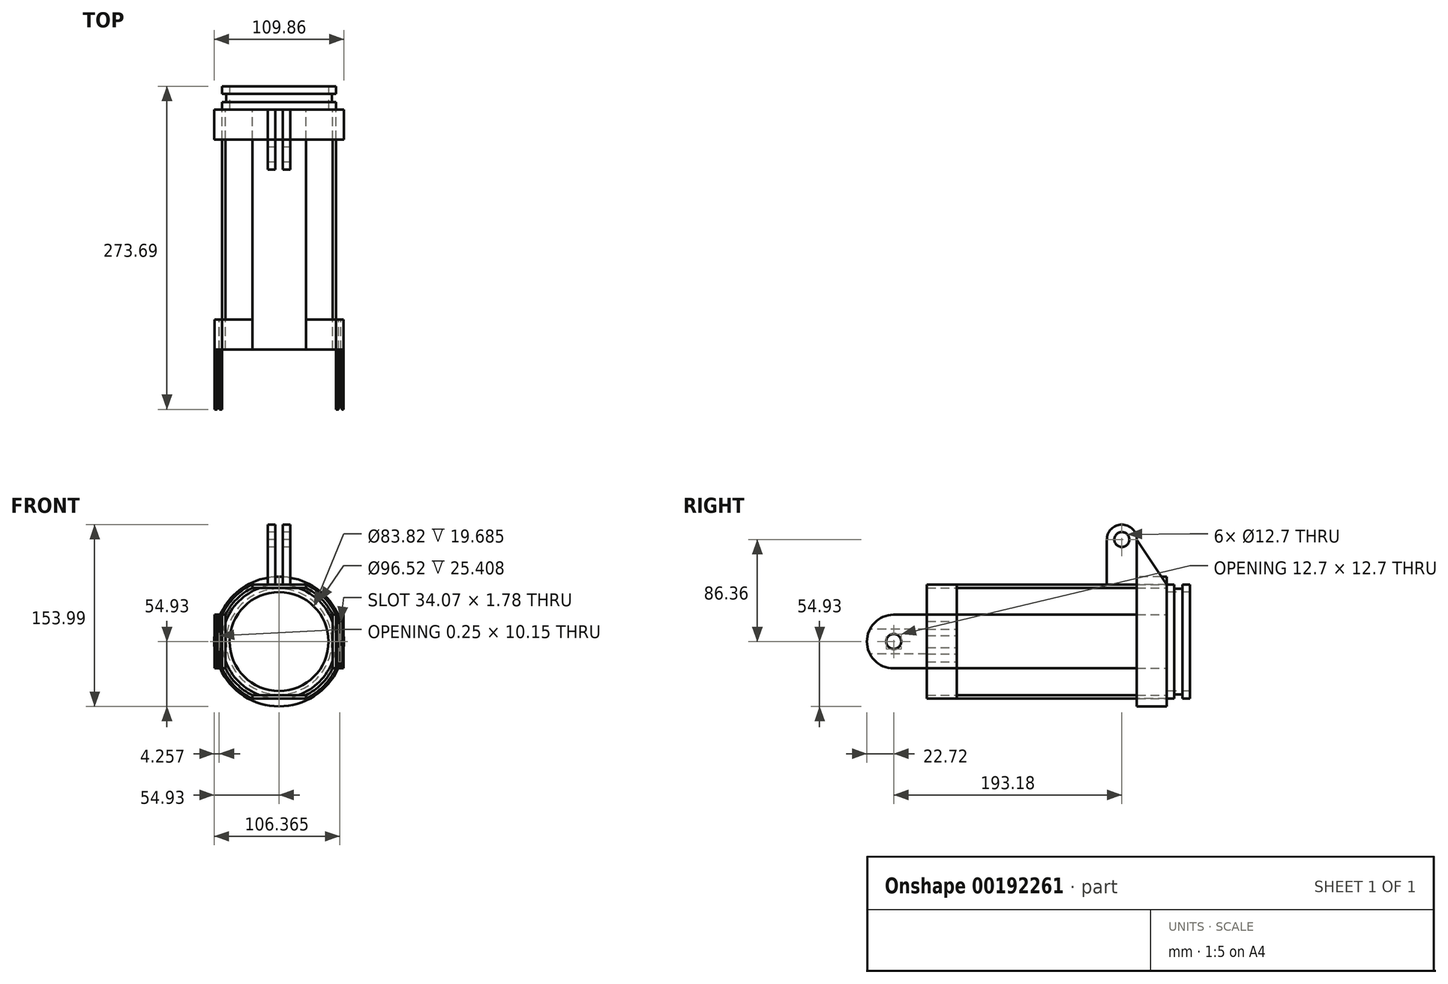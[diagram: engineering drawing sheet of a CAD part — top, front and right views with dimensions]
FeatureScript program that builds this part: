
annotation { "Feature Type Name" : "Feature", "Feature Type Description" : "" }
export const myFeature = defineFeature(function(context is Context, id is Id, definition is map)
    precondition{}
    {
        {
            var Q0;
            Q0=qCreatedBy(makeId("Front.planeOp"),FACE);
            var sketch = newSketch(context, id + "F0", { "sketchPlane" : qUnion([Q0])});
            skCircle(sketch, "E0", {"center": v(0, 0) * mm, "radius": 50.8 * mm});
            skCircle(sketch, "E1", {"center": v(0, 0) * mm, "radius": 53.34 * mm});
            skLineSegment(sketch, "E2", {"start": v(0, -48.26) * mm, "end": v(22.72, -48.26) * mm});
            skLineSegment(sketch, "E3", {"start": v(22.72, -48.26) * mm, "end": v(22.72, -45.44) * mm});
            skLineSegment(sketch, "E4", {"start": v(22.72, -45.44) * mm, "end": v(-22.72, -45.44) * mm});
            skLineSegment(sketch, "E5", {"start": v(-22.72, -45.44) * mm, "end": v(-22.72, -48.26) * mm});
            skLineSegment(sketch, "E6", {"start": v(-22.72, -48.26) * mm, "end": v(0, -48.26) * mm});
            skLineSegment(sketch, "E7", {"start": v(-48.26, 0) * mm, "end": v(-48.26, -22.72) * mm});
            skLineSegment(sketch, "E8", {"start": v(-48.26, -22.72) * mm, "end": v(-45.44, -22.72) * mm});
            skLineSegment(sketch, "E9", {"start": v(-45.44, -22.72) * mm, "end": v(-45.44, 22.72) * mm});
            skLineSegment(sketch, "E10", {"start": v(-45.44, 22.72) * mm, "end": v(-48.26, 22.72) * mm});
            skLineSegment(sketch, "E11", {"start": v(-48.26, 22.72) * mm, "end": v(-48.26, 0) * mm});
            skLineSegment(sketch, "E12", {"start": v(48.26, 0) * mm, "end": v(48.26, -22.72) * mm});
            skLineSegment(sketch, "E13", {"start": v(48.26, -22.72) * mm, "end": v(45.44, -22.72) * mm});
            skLineSegment(sketch, "E14", {"start": v(45.44, -22.72) * mm, "end": v(45.44, 22.72) * mm});
            skLineSegment(sketch, "E15", {"start": v(45.44, 22.72) * mm, "end": v(48.26, 22.72) * mm});
            skLineSegment(sketch, "E16", {"start": v(48.26, 22.72) * mm, "end": v(48.26, 0) * mm});
            skLineSegment(sketch, "E17", {"start": v(0, 50.8) * mm, "end": v(0, 48.26) * mm});
            skLineSegment(sketch, "E18", {"start": v(0, 48.26) * mm, "end": v(22.72, 48.26) * mm});
            skLineSegment(sketch, "E19", {"start": v(22.72, 48.26) * mm, "end": v(22.72, 45.44) * mm});
            skLineSegment(sketch, "E20", {"start": v(22.72, 45.44) * mm, "end": v(-22.72, 45.44) * mm});
            skLineSegment(sketch, "E21", {"start": v(-22.72, 45.44) * mm, "end": v(-22.72, 48.26) * mm});
            skLineSegment(sketch, "E22", {"start": v(-22.72, 48.26) * mm, "end": v(0, 48.26) * mm});
            skLineSegment(sketch, "E23", {"start": v(-48.26, -22.72) * mm, "end": v(-50.55, -22.72) * mm});
            skLineSegment(sketch, "E24", {"start": v(-50.55, -22.72) * mm, "end": v(-50.55, 22.72) * mm});
            skLineSegment(sketch, "E25", {"start": v(-50.55, 22.72) * mm, "end": v(-48.26, 22.72) * mm});
            skLineSegment(sketch, "E26", {"start": v(-50.55, 22.72) * mm, "end": v(-52.32, 22.72) * mm});
            skLineSegment(sketch, "E27", {"start": v(-52.32, 22.72) * mm, "end": v(-52.32, -22.72) * mm});
            skLineSegment(sketch, "E28", {"start": v(-52.32, -22.72) * mm, "end": v(-50.55, -22.72) * mm});
            skLineSegment(sketch, "E29", {"start": v(48.26, -22.72) * mm, "end": v(50.55, -22.72) * mm});
            skLineSegment(sketch, "E30", {"start": v(50.55, -22.72) * mm, "end": v(50.55, 22.72) * mm});
            skLineSegment(sketch, "E31", {"start": v(50.55, 22.72) * mm, "end": v(48.26, 22.72) * mm});
            skLineSegment(sketch, "E32", {"start": v(50.55, 22.72) * mm, "end": v(52.32, 22.72) * mm});
            skLineSegment(sketch, "E33", {"start": v(52.32, 22.72) * mm, "end": v(52.32, -22.72) * mm});
            skLineSegment(sketch, "E34", {"start": v(52.32, -22.72) * mm, "end": v(50.55, -22.72) * mm});
            skLineSegment(sketch, "E35", {"start": v(48.26, 0) * mm, "end": v(0, 0) * mm});
            skLineSegment(sketch, "E36.bottom", {"start": v(52.32, -22.72) * mm, "end": v(54.61, -22.72) * mm});
            skLineSegment(sketch, "E36.top", {"start": v(52.32, 22.72) * mm, "end": v(54.61, 22.72) * mm});
            skLineSegment(sketch, "E36.left", {"start": v(52.32, -22.72) * mm, "end": v(52.32, 22.72) * mm});
            skLineSegment(sketch, "E36.right", {"start": v(54.61, -22.72) * mm, "end": v(54.6, 22.72) * mm});
            skLineSegment(sketch, "E37.bottom", {"start": v(54.61, -22.72) * mm, "end": v(56.13, -22.72) * mm});
            skLineSegment(sketch, "E37.top", {"start": v(54.61, 22.72) * mm, "end": v(56.13, 22.72) * mm});
            skLineSegment(sketch, "E37.right", {"start": v(56.13, -22.72) * mm, "end": v(56.13, 22.72) * mm});
            skLineSegment(sketch, "E38.bottom", {"start": v(-52.32, 22.72) * mm, "end": v(-54.61, 22.72) * mm});
            skLineSegment(sketch, "E38.top", {"start": v(-52.32, -22.72) * mm, "end": v(-54.61, -22.72) * mm});
            skLineSegment(sketch, "E38.right", {"start": v(-54.61, 22.72) * mm, "end": v(-54.6, -22.72) * mm});
            skLineSegment(sketch, "E39.bottom", {"start": v(-54.61, 22.72) * mm, "end": v(-56.13, 22.72) * mm});
            skLineSegment(sketch, "E39.top", {"start": v(-54.61, -22.72) * mm, "end": v(-56.13, -22.72) * mm});
            skLineSegment(sketch, "E39.right", {"start": v(-56.13, 22.72) * mm, "end": v(-56.13, -22.72) * mm});
            skSolve(sketch);
        }
        {
            var Q0;
            {var subQ0=sQuery(id+"F0.wireOp",EDGE,"E5");Q0=makeQuery(id+"F0.imprint","IMPRINT",FACE,{"disambiguationData":[TD([[makeQuery(id+"F0.imprint","IMPRINT",EDGE,{"derivedFrom":subQ0}),-1.0]])]});}
            var Q1;
            {var subQ0=sQuery(id+"F0.wireOp",EDGE,"E3");Q1=makeQuery(id+"F0.imprint","IMPRINT",FACE,{"disambiguationData":[TD([[makeQuery(id+"F0.imprint","IMPRINT",EDGE,{"derivedFrom":subQ0}),-1.0]])]});}
            var Q2;
            {var subQ0=sQuery(id+"F0.wireOp",EDGE,"E10");Q2=makeQuery(id+"F0.imprint","IMPRINT",FACE,{"disambiguationData":[TD([[makeQuery(id+"F0.imprint","IMPRINT",EDGE,{"derivedFrom":subQ0}),-1.0]])]});}
            var Q3;
            {var subQ0=sQuery(id+"F0.wireOp",EDGE,"E15");Q3=makeQuery(id+"F0.imprint","IMPRINT",FACE,{"disambiguationData":[TD([[makeQuery(id+"F0.imprint","IMPRINT",EDGE,{"derivedFrom":subQ0}),1.0]])]});}
            extrude(context, id + "F1", {"entities" : qUnion([Q0, Q1, Q2, Q3]), "depth" : 25.4 * mm});
        }
        {
            var Q0;
            {var subQ0=sQuery(id+"F0.wireOp",EDGE,"E20");Q0=makeQuery(id+"F0.imprint","IMPRINT",FACE,{"disambiguationData":[TD([[makeQuery(id+"F0.imprint","IMPRINT",EDGE,{"derivedFrom":subQ0}),-1.0]])]});}
            var Q1;
            {var subQ0=sQuery(id+"F0.wireOp",EDGE,"E21");Q1=makeQuery(id+"F0.imprint","IMPRINT",FACE,{"disambiguationData":[TD([[makeQuery(id+"F0.imprint","IMPRINT",EDGE,{"derivedFrom":subQ0}),-1.0]])]});}
            var Q2;
            {var subQ0=sQuery(id+"F0.wireOp",EDGE,"E19");Q2=makeQuery(id+"F0.imprint","IMPRINT",FACE,{"disambiguationData":[TD([[makeQuery(id+"F0.imprint","IMPRINT",EDGE,{"derivedFrom":subQ0}),-1.0]])]});}
            var Q3;
            {var subQ0=sQuery(id+"F0.wireOp",EDGE,"E15");Q3=makeQuery(id+"F0.imprint","IMPRINT",FACE,{"disambiguationData":[TD([[makeQuery(id+"F0.imprint","IMPRINT",EDGE,{"derivedFrom":subQ0}),-1.0]])]});}
            var Q4;
            {var subQ5=sQuery(id+"F0.wireOp",EDGE,"E14");Q4=makeQuery(id+"F0.imprint","IMPRINT",FACE,{"disambiguationData":[TD([[makeQuery(id+"F0.imprint","IMPRINT",EDGE,{"derivedFrom":subQ5}),-1.0]])]});}
            var Q5;
            {var subQ0=sQuery(id+"F0.wireOp",EDGE,"E13");Q5=makeQuery(id+"F0.imprint","IMPRINT",FACE,{"disambiguationData":[TD([[makeQuery(id+"F0.imprint","IMPRINT",EDGE,{"derivedFrom":subQ0}),-1.0]])]});}
            var Q6;
            {var subQ0=sQuery(id+"F0.wireOp",EDGE,"E3");Q6=makeQuery(id+"F0.imprint","IMPRINT",FACE,{"disambiguationData":[TD([[makeQuery(id+"F0.imprint","IMPRINT",EDGE,{"derivedFrom":subQ0}),1.0]])]});}
            var Q7;
            {var subQ0=sQuery(id+"F0.wireOp",EDGE,"E4");Q7=makeQuery(id+"F0.imprint","IMPRINT",FACE,{"disambiguationData":[TD([[makeQuery(id+"F0.imprint","IMPRINT",EDGE,{"derivedFrom":subQ0}),1.0]])]});}
            var Q8;
            {var subQ0=sQuery(id+"F0.wireOp",EDGE,"E5");Q8=makeQuery(id+"F0.imprint","IMPRINT",FACE,{"disambiguationData":[TD([[makeQuery(id+"F0.imprint","IMPRINT",EDGE,{"derivedFrom":subQ0}),1.0]])]});}
            var Q9;
            {var subQ0=sQuery(id+"F0.wireOp",EDGE,"E8");Q9=makeQuery(id+"F0.imprint","IMPRINT",FACE,{"disambiguationData":[TD([[makeQuery(id+"F0.imprint","IMPRINT",EDGE,{"derivedFrom":subQ0}),1.0]])]});}
            var Q10;
            {var subQ0=sQuery(id+"F0.wireOp",EDGE,"E9");Q10=makeQuery(id+"F0.imprint","IMPRINT",FACE,{"disambiguationData":[TD([[makeQuery(id+"F0.imprint","IMPRINT",EDGE,{"derivedFrom":subQ0}),1.0]])]});}
            var Q11;
            {var subQ0=sQuery(id+"F0.wireOp",EDGE,"E10");Q11=makeQuery(id+"F0.imprint","IMPRINT",FACE,{"disambiguationData":[TD([[makeQuery(id+"F0.imprint","IMPRINT",EDGE,{"derivedFrom":subQ0}),1.0]])]});}
            extrude(context, id + "F2", {"entities" : qUnion([Q0, Q1, Q2, Q3, Q4, Q5, Q6, Q7, Q8, Q9, Q10, Q11]), "depth" : 203.2 * mm});
        }
        {
            var Q0;
            {var subQ0=sQuery(id+"F0.wireOp",EDGE,"E11");var subQ1=sQuery(id+"F0.wireOp",EDGE,"E0");var subQ2=makeQuery(id+"F0.imprint","INTERSECT",VERTEX,{"derivedFrom":[subQ1,subQ0]});Q0=makeQuery(id+"F0.imprint","IMPRINT",FACE,{"disambiguationData":[TD([[makeQuery(id+"F0.imprint","IMPRINT",EDGE,{"disambiguationData":[TD([[subQ2,-1.0]])],"derivedFrom":subQ1}),1.0]])]});}
            var Q1;
            {var subQ3=sQuery(id+"F0.wireOp",EDGE,"E0");var subQ6=sQuery(id+"F0.wireOp",EDGE,"E11");var subQ8=makeQuery(id+"F0.imprint","INTERSECT",VERTEX,{"derivedFrom":[subQ3,subQ6]});Q1=makeQuery(id+"F0.imprint","IMPRINT",FACE,{"disambiguationData":[TD([[makeQuery(id+"F0.imprint","IMPRINT",EDGE,{"disambiguationData":[TD([[subQ8,-1.0]])],"derivedFrom":subQ3}),-1.0]])]});}
            var Q2;
            {var subQ0=sQuery(id+"F0.wireOp",EDGE,"E26");Q2=makeQuery(id+"F0.imprint","IMPRINT",FACE,{"disambiguationData":[TD([[makeQuery(id+"F0.imprint","IMPRINT",EDGE,{"derivedFrom":subQ0}),1.0]])]});}
            var Q3;
            {var subQ0=sQuery(id+"F0.wireOp",EDGE,"E23");Q3=makeQuery(id+"F0.imprint","IMPRINT",FACE,{"disambiguationData":[TD([[makeQuery(id+"F0.imprint","IMPRINT",EDGE,{"derivedFrom":subQ0}),-1.0]])]});}
            var Q4;
            {var subQ0=sQuery(id+"F0.wireOp",EDGE,"E25");Q4=makeQuery(id+"F0.imprint","IMPRINT",FACE,{"disambiguationData":[TD([[makeQuery(id+"F0.imprint","IMPRINT",EDGE,{"derivedFrom":subQ0}),-1.0]])]});}
            var Q5;
            {var subQ0=sQuery(id+"F0.wireOp",EDGE,"E29");Q5=makeQuery(id+"F0.imprint","IMPRINT",FACE,{"disambiguationData":[TD([[makeQuery(id+"F0.imprint","IMPRINT",EDGE,{"derivedFrom":subQ0}),1.0]])]});}
            var Q6;
            {var subQ0=sQuery(id+"F0.wireOp",EDGE,"E32");Q6=makeQuery(id+"F0.imprint","IMPRINT",FACE,{"disambiguationData":[TD([[makeQuery(id+"F0.imprint","IMPRINT",EDGE,{"derivedFrom":subQ0}),-1.0]])]});}
            var Q7;
            {var subQ3=sQuery(id+"F0.wireOp",EDGE,"E0");var subQ6=sQuery(id+"F0.wireOp",EDGE,"E16");var subQ8=makeQuery(id+"F0.imprint","INTERSECT",VERTEX,{"derivedFrom":[subQ3,subQ6]});Q7=makeQuery(id+"F0.imprint","IMPRINT",FACE,{"disambiguationData":[TD([[makeQuery(id+"F0.imprint","IMPRINT",EDGE,{"disambiguationData":[TD([[subQ8,1.0]])],"derivedFrom":subQ3}),-1.0]])]});}
            var Q8;
            {var subQ0=sQuery(id+"F0.wireOp",EDGE,"E16");var subQ1=sQuery(id+"F0.wireOp",EDGE,"E0");var subQ2=makeQuery(id+"F0.imprint","INTERSECT",VERTEX,{"derivedFrom":[subQ1,subQ0]});Q8=makeQuery(id+"F0.imprint","IMPRINT",FACE,{"disambiguationData":[TD([[makeQuery(id+"F0.imprint","IMPRINT",EDGE,{"disambiguationData":[TD([[subQ2,1.0]])],"derivedFrom":subQ1}),1.0]])]});}
            var Q9;
            {var subQ0=sQuery(id+"F0.wireOp",EDGE,"E31");Q9=makeQuery(id+"F0.imprint","IMPRINT",FACE,{"disambiguationData":[TD([[makeQuery(id+"F0.imprint","IMPRINT",EDGE,{"derivedFrom":subQ0}),1.0]])]});}
            var Q10;
            {var subQ0=sQuery(id+"F0.wireOp",EDGE,"E1");var subQ1=makeQuery(id+"F0.imprint","INTERSECT",VERTEX,{"derivedFrom":[subQ0,sQuery(id+"F0.wireOp",EDGE,"E33")]});Q10=makeQuery(id+"F0.imprint","IMPRINT",FACE,{"disambiguationData":[TD([[makeQuery(id+"F0.imprint","IMPRINT",EDGE,{"disambiguationData":[TD([[subQ1,-1.0]])],"derivedFrom":subQ0}),1.0]])]});}
            var Q11;
            {var subQ0=sQuery(id+"F0.wireOp",EDGE,"E30");var subQ1=sQuery(id+"F0.wireOp",EDGE,"E0");var subQ2=makeQuery(id+"F0.imprint","INTERSECT",VERTEX,{"derivedFrom":[subQ1,subQ0]});Q11=makeQuery(id+"F0.imprint","IMPRINT",FACE,{"disambiguationData":[TD([[makeQuery(id+"F0.imprint","IMPRINT",EDGE,{"disambiguationData":[TD([[subQ2,1.0]])],"derivedFrom":subQ1}),-1.0]])]});}
            var Q12;
            {var subQ5=sQuery(id+"F0.wireOp",EDGE,"E34");Q12=makeQuery(id+"F0.imprint","IMPRINT",FACE,{"disambiguationData":[TD([[makeQuery(id+"F0.imprint","IMPRINT",EDGE,{"derivedFrom":subQ5}),-1.0]])]});}
            var Q13;
            {var subQ0=sQuery(id+"F0.wireOp",EDGE,"E24");var subQ1=sQuery(id+"F0.wireOp",EDGE,"E0");var subQ2=makeQuery(id+"F0.imprint","INTERSECT",VERTEX,{"derivedFrom":[subQ1,subQ0]});Q13=makeQuery(id+"F0.imprint","IMPRINT",FACE,{"disambiguationData":[TD([[makeQuery(id+"F0.imprint","IMPRINT",EDGE,{"disambiguationData":[TD([[subQ2,-1.0]])],"derivedFrom":subQ1}),-1.0]])]});}
            var Q14;
            {var subQ0=sQuery(id+"F0.wireOp",EDGE,"E1");var subQ1=makeQuery(id+"F0.imprint","INTERSECT",VERTEX,{"derivedFrom":[subQ0,sQuery(id+"F0.wireOp",EDGE,"E27")]});Q14=makeQuery(id+"F0.imprint","IMPRINT",FACE,{"disambiguationData":[TD([[makeQuery(id+"F0.imprint","IMPRINT",EDGE,{"disambiguationData":[TD([[subQ1,1.0]])],"derivedFrom":subQ0}),1.0]])]});}
            var Q15;
            {var subQ5=sQuery(id+"F0.wireOp",EDGE,"E28");Q15=makeQuery(id+"F0.imprint","IMPRINT",FACE,{"disambiguationData":[TD([[makeQuery(id+"F0.imprint","IMPRINT",EDGE,{"derivedFrom":subQ5}),1.0]])]});}
            var Q16;
            {var subQ0=sQuery(id+"F0.wireOp",EDGE,"E36.left");var subQ1=sQuery(id+"F0.wireOp",EDGE,"E1");var subQ2=makeQuery(id+"F0.imprint","INTERSECT",VERTEX,{"disambiguationData":[OD(0.0)],"derivedFrom":[subQ1,subQ0]});Q16=makeQuery(id+"F0.imprint","IMPRINT",FACE,{"disambiguationData":[TD([[makeQuery(id+"F0.imprint","IMPRINT",EDGE,{"disambiguationData":[TD([[subQ2,1.0]])],"derivedFrom":subQ1}),1.0]])]});}
            var Q17;
            {var subQ1=sQuery(id+"F0.wireOp",EDGE,"E38.bottom");Q17=makeQuery(id+"F0.imprint","IMPRINT",FACE,{"disambiguationData":[TD([[makeQuery(id+"F0.imprint","IMPRINT",EDGE,{"derivedFrom":subQ1}),1.0]])]});}
            var Q18;
            {var subQ0=sQuery(id+"F0.wireOp",EDGE,"E27");var subQ1=sQuery(id+"F0.wireOp",EDGE,"E1");var subQ2=makeQuery(id+"F0.imprint","INTERSECT",VERTEX,{"disambiguationData":[OD(0.0)],"derivedFrom":[subQ1,subQ0]});Q18=makeQuery(id+"F0.imprint","IMPRINT",FACE,{"disambiguationData":[TD([[makeQuery(id+"F0.imprint","IMPRINT",EDGE,{"disambiguationData":[TD([[subQ2,-1.0]])],"derivedFrom":subQ1}),1.0]])]});}
            var Q19;
            {var subQ0=sQuery(id+"F0.wireOp",EDGE,"E36.left");var subQ1=sQuery(id+"F0.wireOp",EDGE,"E1");var subQ2=makeQuery(id+"F0.imprint","INTERSECT",VERTEX,{"disambiguationData":[OD(0.0)],"derivedFrom":[subQ1,subQ0]});Q19=makeQuery(id+"F0.imprint","IMPRINT",FACE,{"disambiguationData":[TD([[makeQuery(id+"F0.imprint","IMPRINT",EDGE,{"disambiguationData":[TD([[subQ2,1.0]])],"derivedFrom":subQ1}),1.0]])]});}
            var Q20;
            {var subQ0=sQuery(id+"F0.wireOp",EDGE,"E30");var subQ1=sQuery(id+"F0.wireOp",EDGE,"E0");var subQ9=makeQuery(id+"F0.imprint","INTERSECT",VERTEX,{"disambiguationData":[OD(0.0)],"derivedFrom":[subQ1,subQ0]});Q20=makeQuery(id+"F0.imprint","IMPRINT",FACE,{"disambiguationData":[TD([[makeQuery(id+"F0.imprint","IMPRINT",EDGE,{"disambiguationData":[TD([[subQ9,1.0]])],"derivedFrom":subQ1}),-1.0]])]});}
            var Q21;
            {var subQ1=sQuery(id+"F0.wireOp",EDGE,"E36.bottom");Q21=makeQuery(id+"F0.imprint","IMPRINT",FACE,{"disambiguationData":[TD([[makeQuery(id+"F0.imprint","IMPRINT",EDGE,{"derivedFrom":subQ1}),1.0]])]});}
            var Q22;
            {var subQ0=sQuery(id+"F0.wireOp",EDGE,"E24");var subQ1=sQuery(id+"F0.wireOp",EDGE,"E0");var subQ9=makeQuery(id+"F0.imprint","INTERSECT",VERTEX,{"disambiguationData":[OD(0.0)],"derivedFrom":[subQ1,subQ0]});Q22=makeQuery(id+"F0.imprint","IMPRINT",FACE,{"disambiguationData":[TD([[makeQuery(id+"F0.imprint","IMPRINT",EDGE,{"disambiguationData":[TD([[subQ9,-1.0]])],"derivedFrom":subQ1}),-1.0]])]});}
            var Q23;
            {var subQ0=sQuery(id+"F0.wireOp",EDGE,"E24");var subQ1=sQuery(id+"F0.wireOp",EDGE,"E0");var subQ2=makeQuery(id+"F0.imprint","INTERSECT",VERTEX,{"disambiguationData":[OD(1.0)],"derivedFrom":[subQ1,subQ0]});Q23=makeQuery(id+"F0.imprint","IMPRINT",FACE,{"disambiguationData":[TD([[makeQuery(id+"F0.imprint","IMPRINT",EDGE,{"disambiguationData":[TD([[subQ2,-1.0]])],"derivedFrom":subQ1}),-1.0]])]});}
            var Q24;
            {var subQ1=sQuery(id+"F0.wireOp",EDGE,"E38.bottom");Q24=makeQuery(id+"F0.imprint","IMPRINT",FACE,{"disambiguationData":[TD([[makeQuery(id+"F0.imprint","IMPRINT",EDGE,{"derivedFrom":subQ1}),1.0]])]});}
            extrude(context, id + "F3", {"entities" : qUnion([Q0, Q1, Q2, Q3, Q4, Q5, Q6, Q7, Q8, Q9, Q10, Q11, Q12, Q13, Q14, Q15, Q16, Q17, Q18, Q19, Q20, Q21, Q22, Q23, Q24]), "depth" : 25.4 * mm});
        }
        {
            var Q0;
            Q0=makeQuery(id+"F1.opExtrude","SWEPT_BODY",BODY,{"disambiguationData":[OSD([sQuery(id+"F0.wireOp",EDGE,"E0"),sQuery(id+"F0.wireOp",EDGE,"E1"),sQuery(id+"F0.wireOp",EDGE,"E15"),sQuery(id+"F0.wireOp",EDGE,"E19")])]});
            var Q1;
            Q1=makeQuery(id+"F1.opExtrude","SWEPT_BODY",BODY,{"disambiguationData":[OSD([sQuery(id+"F0.wireOp",EDGE,"E0"),sQuery(id+"F0.wireOp",EDGE,"E1"),sQuery(id+"F0.wireOp",EDGE,"E3"),sQuery(id+"F0.wireOp",EDGE,"E13")])]});
            var Q2;
            Q2=makeQuery(id+"F1.opExtrude","SWEPT_BODY",BODY,{"disambiguationData":[OSD([sQuery(id+"F0.wireOp",EDGE,"E0"),sQuery(id+"F0.wireOp",EDGE,"E1"),sQuery(id+"F0.wireOp",EDGE,"E5"),sQuery(id+"F0.wireOp",EDGE,"E8")])]});
            var Q3;
            Q3=makeQuery(id+"F1.opExtrude","SWEPT_BODY",BODY,{"disambiguationData":[OSD([sQuery(id+"F0.wireOp",EDGE,"E0"),sQuery(id+"F0.wireOp",EDGE,"E1"),sQuery(id+"F0.wireOp",EDGE,"E10"),sQuery(id+"F0.wireOp",EDGE,"E21")])]});
            transform(context, id + "F4", {"entities" : qUnion([Q0, Q1, Q2, Q3]), "transformType" : TransformType.TRANSLATION_3D, "dx" : 0 * mm, "dy" : -177.8 * mm, "dz" : 0 * mm, "makeCopy" : true});
        }
        {
            var Q0;
            Q0=qCreatedBy(makeId("Right.planeOp"),FACE);
            var sketch = newSketch(context, id + "F5", { "sketchPlane" : qUnion([Q0])});
            skLineSegment(sketch, "E40", {"start": v(0, 0) * mm, "end": v(28.08, 0) * mm});
            skCircle(sketch, "E41", {"center": v(28.08, 0) * mm, "radius": 6.35 * mm});
            skCircle(sketch, "E42", {"center": v(28.08, 0) * mm, "radius": 22.72 * mm});
            skLineSegment(sketch, "E43", {"start": v(0, 0) * mm, "end": v(0, -22.72) * mm});
            skLineSegment(sketch, "E44.bottom", {"start": v(0, -22.72) * mm, "end": v(50.8, -22.72) * mm});
            skLineSegment(sketch, "E44.top", {"start": v(0, 22.72) * mm, "end": v(50.8, 22.72) * mm});
            skLineSegment(sketch, "E44.left", {"start": v(0, -22.72) * mm, "end": v(0, 22.72) * mm});
            skLineSegment(sketch, "E44.right", {"start": v(50.8, -22.72) * mm, "end": v(50.8, 22.72) * mm});
            skLineSegment(sketch, "E45", {"start": v(0, 0) * mm, "end": v(-231.28, 0) * mm});
            skCircle(sketch, "E46", {"center": v(-231.28, 0) * mm, "radius": 22.72 * mm});
            skCircle(sketch, "E47", {"center": v(-231.28, 0) * mm, "radius": 6.35 * mm});
            skLineSegment(sketch, "E48", {"start": v(-231.28, 0) * mm, "end": v(-203.19, 0) * mm});
            skLineSegment(sketch, "E49", {"start": v(-203.19, 0) * mm, "end": v(-203.19, 22.72) * mm});
            skLineSegment(sketch, "E50.bottom", {"start": v(-203.19, 22.72) * mm, "end": v(-254.24, 22.72) * mm});
            skLineSegment(sketch, "E50.top", {"start": v(-203.19, -22.72) * mm, "end": v(-254.24, -22.72) * mm});
            skLineSegment(sketch, "E50.left", {"start": v(-203.19, 22.72) * mm, "end": v(-203.19, -22.72) * mm});
            skLineSegment(sketch, "E50.right", {"start": v(-254.24, 22.72) * mm, "end": v(-254.24, -22.72) * mm});
            skLineSegment(sketch, "E51", {"start": v(0, 0) * mm, "end": v(0, 48.26) * mm});
            skLineSegment(sketch, "E52", {"start": v(0, 48.26) * mm, "end": v(-25.4, 48.26) * mm});
            skLineSegment(sketch, "E53", {"start": v(-25.4, 48.26) * mm, "end": v(-38.1, 48.26) * mm});
            skLineSegment(sketch, "E54", {"start": v(-38.1, 48.26) * mm, "end": v(-38.1, 86.36) * mm});
            skLineSegment(sketch, "E55.bottom", {"start": v(-25.4, 48.26) * mm, "end": v(-50.8, 48.26) * mm});
            skLineSegment(sketch, "E55.top", {"start": v(-25.4, 99.06) * mm, "end": v(-50.8, 99.06) * mm});
            skLineSegment(sketch, "E55.left", {"start": v(-25.4, 48.26) * mm, "end": v(-25.4, 99.06) * mm});
            skLineSegment(sketch, "E55.right", {"start": v(-50.8, 48.26) * mm, "end": v(-50.8, 99.06) * mm});
            skCircle(sketch, "E56", {"center": v(-38.1, 86.36) * mm, "radius": 6.35 * mm});
            skCircle(sketch, "E57", {"center": v(-38.1, 86.36) * mm, "radius": 12.7 * mm});
            skCircle(sketch, "E58", {"center": v(-231.28, 0) * mm, "radius": 5.56 * mm});
            skLineSegment(sketch, "E59", {"start": v(-38.1, 48.26) * mm, "end": v(-25.4, 48.26) * mm});
            skLineSegment(sketch, "E60", {"start": v(-38.1, 86.36) * mm, "end": v(-25.4, 86.36) * mm});
            skLineSegment(sketch, "E61", {"start": v(-25.4, 86.36) * mm, "end": v(0, 48.26) * mm});
            skSolve(sketch);
        }
        {
            var Q0;
            Q0=makeQuery(id+"F5.imprint","IMPRINT",FACE,{"disambiguationData":[TD([[makeQuery(id+"F5.imprint","IMPRINT",EDGE,{"derivedFrom":sQuery(id+"F5.wireOp",EDGE,"E41")}),1.0]])]});
            var Q1;
            {var subQ0=sQuery(id+"F5.wireOp",EDGE,"E44.top");var subQ1=sQuery(id+"F5.wireOp",EDGE,"E42");var subQ2=makeQuery(id+"F5.imprint","INTERSECT",VERTEX,{"derivedFrom":[subQ1,subQ0]});Q1=makeQuery(id+"F5.imprint","IMPRINT",FACE,{"disambiguationData":[TD([[makeQuery(id+"F5.imprint","IMPRINT",EDGE,{"disambiguationData":[TD([[subQ2,1.0]])],"derivedFrom":subQ1}),-1.0]])]});}
            var Q2;
            {var subQ0=sQuery(id+"F5.wireOp",EDGE,"E44.right");var subQ1=sQuery(id+"F5.wireOp",EDGE,"E42");var subQ2=makeQuery(id+"F5.imprint","INTERSECT",VERTEX,{"derivedFrom":[subQ1,subQ0]});Q2=makeQuery(id+"F5.imprint","IMPRINT",FACE,{"disambiguationData":[TD([[makeQuery(id+"F5.imprint","IMPRINT",EDGE,{"disambiguationData":[TD([[subQ2,1.0]])],"derivedFrom":subQ1}),-1.0]])]});}
            extrude(context, id + "F6", {"entities" : qUnion([Q0, Q1, Q2]), "endBound" : BoundingType.SYMMETRIC, "depth" : 127 * mm});
        }
        {
            var Q0;
            Q0=makeQuery(id+"F3.opExtrude","SWEPT_BODY",BODY,{"disambiguationData":[OSD([sQuery(id+"F0.wireOp",EDGE,"E12"),sQuery(id+"F0.wireOp",EDGE,"E16"),sQuery(id+"F0.wireOp",EDGE,"E29"),sQuery(id+"F0.wireOp",EDGE,"E31"),sQuery(id+"F0.wireOp",EDGE,"E32"),sQuery(id+"F0.wireOp",EDGE,"E33"),sQuery(id+"F0.wireOp",EDGE,"E34")])]});
            var Q1;
            Q1=makeQuery(id+"F3.opExtrude","SWEPT_BODY",BODY,{"disambiguationData":[OSD([sQuery(id+"F0.wireOp",EDGE,"E7"),sQuery(id+"F0.wireOp",EDGE,"E11"),sQuery(id+"F0.wireOp",EDGE,"E23"),sQuery(id+"F0.wireOp",EDGE,"E25"),sQuery(id+"F0.wireOp",EDGE,"E26"),sQuery(id+"F0.wireOp",EDGE,"E27"),sQuery(id+"F0.wireOp",EDGE,"E28")])]});
            transform(context, id + "F7", {"entities" : qUnion([Q0, Q1]), "transformType" : TransformType.TRANSLATION_3D, "dx" : 0 * mm, "dy" : -177.8 * mm, "dz" : 0 * mm, "makeCopy" : true});
        }
        {
            var Q0;
            {var subQ5=sQuery(id+"F5.wireOp",EDGE,"E50.right");Q0=makeQuery(id+"F5.imprint","IMPRINT",FACE,{"disambiguationData":[TD([[makeQuery(id+"F5.imprint","IMPRINT",EDGE,{"derivedFrom":subQ5}),1.0]])]});}
            var Q1;
            {var subQ5=sQuery(id+"F5.wireOp",EDGE,"E50.right");Q1=makeQuery(id+"F5.imprint","IMPRINT",FACE,{"disambiguationData":[TD([[makeQuery(id+"F5.imprint","IMPRINT",EDGE,{"derivedFrom":subQ5}),1.0]])]});}
            var Q2;
            Q2=makeQuery(id+"F5.imprint","IMPRINT",FACE,{"disambiguationData":[TD([[makeQuery(id+"F5.imprint","IMPRINT",EDGE,{"derivedFrom":sQuery(id+"F5.wireOp",EDGE,"E47")}),1.0]])]});
            var Q3;
            Q3=makeQuery(id+"F5.imprint","IMPRINT",FACE,{"disambiguationData":[TD([[makeQuery(id+"F5.imprint","IMPRINT",EDGE,{"derivedFrom":sQuery(id+"F5.wireOp",EDGE,"E58")}),1.0]])]});
            extrude(context, id + "F8", {"entities" : qUnion([Q0, Q1, Q2, Q3]), "endBound" : BoundingType.SYMMETRIC, "depth" : 127 * mm});
        }
        {
            var Q0;
            Q0=qCreatedBy(makeId("Top.planeOp"),FACE);
            var sketch = newSketch(context, id + "F9", { "sketchPlane" : qUnion([Q0])});
            skLineSegment(sketch, "E62", {"start": v(0, 0) * mm, "end": v(0, -25.4) * mm});
            skLineSegment(sketch, "E63", {"start": v(-3.18, -25.4) * mm, "end": v(0, -25.4) * mm});
            skLineSegment(sketch, "E64", {"start": v(0, -25.4) * mm, "end": v(3.18, -25.4) * mm});
            skLineSegment(sketch, "E65.bottom", {"start": v(3.18, -25.4) * mm, "end": v(9.53, -25.4) * mm});
            skLineSegment(sketch, "E65.top", {"start": v(3.18, -50.8) * mm, "end": v(9.53, -50.8) * mm});
            skLineSegment(sketch, "E65.left", {"start": v(3.18, -25.4) * mm, "end": v(3.18, -50.8) * mm});
            skLineSegment(sketch, "E65.right", {"start": v(9.53, -25.4) * mm, "end": v(9.53, -50.8) * mm});
            skLineSegment(sketch, "E66.bottom", {"start": v(-3.18, -25.4) * mm, "end": v(-9.53, -25.4) * mm});
            skLineSegment(sketch, "E66.top", {"start": v(-3.17, -50.8) * mm, "end": v(-9.52, -50.8) * mm});
            skLineSegment(sketch, "E66.left", {"start": v(-3.18, -25.4) * mm, "end": v(-3.17, -50.8) * mm});
            skLineSegment(sketch, "E66.right", {"start": v(-9.53, -25.4) * mm, "end": v(-9.52, -50.8) * mm});
            skSolve(sketch);
        }
        {
            var Q0;
            Q0=makeQuery(id+"F9.imprint","IMPRINT",FACE,{"disambiguationData":[TD([[makeQuery(id+"F9.imprint","IMPRINT",EDGE,{"derivedFrom":sQuery(id+"F9.wireOp",EDGE,"E66.bottom")}),1.0]])]});
            var Q1;
            Q1=makeQuery(id+"F9.imprint","IMPRINT",FACE,{"disambiguationData":[TD([[makeQuery(id+"F9.imprint","IMPRINT",EDGE,{"derivedFrom":sQuery(id+"F9.wireOp",EDGE,"E65.bottom")}),-1.0]])]});
            extrude(context, id + "F10", {"entities" : qUnion([Q0, Q1]), "depth" : 50.8 * mm});
        }
        {
            var Q0;
            Q0=makeQuery(id+"F10.opExtrude","SWEPT_BODY",BODY,{"disambiguationData":[OSD([sQuery(id+"F9.wireOp",EDGE,"E65.bottom"),sQuery(id+"F9.wireOp",EDGE,"E65.top"),sQuery(id+"F9.wireOp",EDGE,"E65.left"),sQuery(id+"F9.wireOp",EDGE,"E65.right")])]});
            var Q1;
            Q1=makeQuery(id+"F10.opExtrude","SWEPT_BODY",BODY,{"disambiguationData":[OSD([sQuery(id+"F9.wireOp",EDGE,"E66.bottom"),sQuery(id+"F9.wireOp",EDGE,"E66.top"),sQuery(id+"F9.wireOp",EDGE,"E66.left"),sQuery(id+"F9.wireOp",EDGE,"E66.right")])]});
            transform(context, id + "F11", {"entities" : qUnion([Q0, Q1]), "transformType" : TransformType.TRANSLATION_3D, "dx" : 0 * mm, "dy" : 0 * mm, "dz" : 48.26 * mm, "makeCopy" : false});
        }
        {
            var Q0;
            Q0=makeQuery(id+"F5.imprint","IMPRINT",FACE,{"disambiguationData":[TD([[makeQuery(id+"F5.imprint","IMPRINT",EDGE,{"derivedFrom":sQuery(id+"F5.wireOp",EDGE,"E56")}),1.0]])]});
            var Q1;
            {var subQ0=sQuery(id+"F5.wireOp",EDGE,"E55.left");var subQ1=sQuery(id+"F5.wireOp",EDGE,"E55.top");var subQ2=makeQuery(id+"F5.imprint","INTERSECT",VERTEX,{"derivedFrom":[subQ1,subQ0]});Q1=makeQuery(id+"F5.imprint","IMPRINT",FACE,{"disambiguationData":[TD([[makeQuery(id+"F5.imprint","IMPRINT",EDGE,{"disambiguationData":[TD([[subQ2,-1.0]])],"derivedFrom":subQ1}),1.0]])]});}
            var Q2;
            {var subQ0=sQuery(id+"F5.wireOp",EDGE,"E55.right");var subQ1=sQuery(id+"F5.wireOp",EDGE,"E55.top");var subQ2=makeQuery(id+"F5.imprint","INTERSECT",VERTEX,{"derivedFrom":[subQ1,subQ0]});Q2=makeQuery(id+"F5.imprint","IMPRINT",FACE,{"disambiguationData":[TD([[makeQuery(id+"F5.imprint","IMPRINT",EDGE,{"disambiguationData":[TD([[subQ2,1.0]])],"derivedFrom":subQ1}),1.0]])]});}
            extrude(context, id + "F12", {"entities" : qUnion([Q0, Q1, Q2]), "endBound" : BoundingType.SYMMETRIC, "depth" : 25.4 * mm});
        }
        {
            var Q0;
            Q0=makeQuery(id+"F12.opExtrude","SWEPT_BODY",BODY,{"disambiguationData":[OSD([sQuery(id+"F5.wireOp",EDGE,"E55.top"),sQuery(id+"F5.wireOp",EDGE,"E55.left"),sQuery(id+"F5.wireOp",EDGE,"E57")])]});
            var Q1;
            Q1=makeQuery(id+"F12.opExtrude","SWEPT_BODY",BODY,{"disambiguationData":[OSD([sQuery(id+"F5.wireOp",EDGE,"E55.top"),sQuery(id+"F5.wireOp",EDGE,"E55.right"),sQuery(id+"F5.wireOp",EDGE,"E57")])]});
            var Q2;
            Q2=makeQuery(id+"F12.opExtrude","SWEPT_BODY",BODY,{"disambiguationData":[OSD([sQuery(id+"F5.wireOp",EDGE,"E56")])]});
            var Q3;
            Q3=makeQuery(id+"F10.opExtrude","SWEPT_BODY",BODY,{"disambiguationData":[OSD([sQuery(id+"F9.wireOp",EDGE,"E65.bottom"),sQuery(id+"F9.wireOp",EDGE,"E65.top"),sQuery(id+"F9.wireOp",EDGE,"E65.left"),sQuery(id+"F9.wireOp",EDGE,"E65.right")])]});
            var Q4;
            Q4=makeQuery(id+"F10.opExtrude","SWEPT_BODY",BODY,{"disambiguationData":[OSD([sQuery(id+"F9.wireOp",EDGE,"E66.bottom"),sQuery(id+"F9.wireOp",EDGE,"E66.top"),sQuery(id+"F9.wireOp",EDGE,"E66.left"),sQuery(id+"F9.wireOp",EDGE,"E66.right")])]});
            booleanBodies(context, id + "F13", {"operationType" : BooleanOperationType.SUBTRACTION, "tools" : qUnion([Q0, Q1, Q2]), "targets" : qUnion([Q3, Q4])});
        }
        {
            var Q0;
            {var subQ0=sQuery(id+"F0.wireOp",EDGE,"E31");Q0=makeQuery(id+"F0.imprint","IMPRINT",FACE,{"disambiguationData":[TD([[makeQuery(id+"F0.imprint","IMPRINT",EDGE,{"derivedFrom":subQ0}),1.0]])]});}
            var Q1;
            {var subQ1=sQuery(id+"F0.wireOp",EDGE,"E36.bottom");Q1=makeQuery(id+"F0.imprint","IMPRINT",FACE,{"disambiguationData":[TD([[makeQuery(id+"F0.imprint","IMPRINT",EDGE,{"derivedFrom":subQ1}),1.0]])]});}
            var Q2;
            {var subQ0=sQuery(id+"F0.wireOp",EDGE,"E16");var subQ1=sQuery(id+"F0.wireOp",EDGE,"E0");var subQ2=makeQuery(id+"F0.imprint","INTERSECT",VERTEX,{"derivedFrom":[subQ1,subQ0]});Q2=makeQuery(id+"F0.imprint","IMPRINT",FACE,{"disambiguationData":[TD([[makeQuery(id+"F0.imprint","IMPRINT",EDGE,{"disambiguationData":[TD([[subQ2,1.0]])],"derivedFrom":subQ1}),-1.0]])]});}
            var Q3;
            {var subQ0=sQuery(id+"F0.wireOp",EDGE,"E16");var subQ1=sQuery(id+"F0.wireOp",EDGE,"E0");var subQ2=makeQuery(id+"F0.imprint","INTERSECT",VERTEX,{"derivedFrom":[subQ1,subQ0]});Q3=makeQuery(id+"F0.imprint","IMPRINT",FACE,{"disambiguationData":[TD([[makeQuery(id+"F0.imprint","IMPRINT",EDGE,{"disambiguationData":[TD([[subQ2,1.0]])],"derivedFrom":subQ1}),1.0]])]});}
            var Q4;
            {var subQ0=sQuery(id+"F0.wireOp",EDGE,"E36.left");var subQ1=sQuery(id+"F0.wireOp",EDGE,"E1");var subQ2=makeQuery(id+"F0.imprint","INTERSECT",VERTEX,{"disambiguationData":[OD(0.0)],"derivedFrom":[subQ1,subQ0]});Q4=makeQuery(id+"F0.imprint","IMPRINT",FACE,{"disambiguationData":[TD([[makeQuery(id+"F0.imprint","IMPRINT",EDGE,{"disambiguationData":[TD([[subQ2,1.0]])],"derivedFrom":subQ1}),1.0]])]});}
            var Q5;
            {var subQ0=sQuery(id+"F0.wireOp",EDGE,"E30");var subQ1=sQuery(id+"F0.wireOp",EDGE,"E0");var subQ2=makeQuery(id+"F0.imprint","INTERSECT",VERTEX,{"derivedFrom":[subQ1,subQ0]});Q5=makeQuery(id+"F0.imprint","IMPRINT",FACE,{"disambiguationData":[TD([[makeQuery(id+"F0.imprint","IMPRINT",EDGE,{"disambiguationData":[TD([[subQ2,1.0]])],"derivedFrom":subQ1}),-1.0]])]});}
            var Q6;
            {var subQ0=sQuery(id+"F0.wireOp",EDGE,"E29");Q6=makeQuery(id+"F0.imprint","IMPRINT",FACE,{"disambiguationData":[TD([[makeQuery(id+"F0.imprint","IMPRINT",EDGE,{"derivedFrom":subQ0}),1.0]])]});}
            var Q7;
            {var subQ1=sQuery(id+"F0.wireOp",EDGE,"E38.bottom");Q7=makeQuery(id+"F0.imprint","IMPRINT",FACE,{"disambiguationData":[TD([[makeQuery(id+"F0.imprint","IMPRINT",EDGE,{"derivedFrom":subQ1}),1.0]])]});}
            var Q8;
            {var subQ0=sQuery(id+"F0.wireOp",EDGE,"E27");var subQ1=sQuery(id+"F0.wireOp",EDGE,"E1");var subQ2=makeQuery(id+"F0.imprint","INTERSECT",VERTEX,{"disambiguationData":[OD(0.0)],"derivedFrom":[subQ1,subQ0]});Q8=makeQuery(id+"F0.imprint","IMPRINT",FACE,{"disambiguationData":[TD([[makeQuery(id+"F0.imprint","IMPRINT",EDGE,{"disambiguationData":[TD([[subQ2,-1.0]])],"derivedFrom":subQ1}),1.0]])]});}
            var Q9;
            {var subQ0=sQuery(id+"F0.wireOp",EDGE,"E11");var subQ1=sQuery(id+"F0.wireOp",EDGE,"E0");var subQ2=makeQuery(id+"F0.imprint","INTERSECT",VERTEX,{"derivedFrom":[subQ1,subQ0]});Q9=makeQuery(id+"F0.imprint","IMPRINT",FACE,{"disambiguationData":[TD([[makeQuery(id+"F0.imprint","IMPRINT",EDGE,{"disambiguationData":[TD([[subQ2,-1.0]])],"derivedFrom":subQ1}),1.0]])]});}
            var Q10;
            {var subQ0=sQuery(id+"F0.wireOp",EDGE,"E11");var subQ1=sQuery(id+"F0.wireOp",EDGE,"E0");var subQ2=makeQuery(id+"F0.imprint","INTERSECT",VERTEX,{"derivedFrom":[subQ1,subQ0]});Q10=makeQuery(id+"F0.imprint","IMPRINT",FACE,{"disambiguationData":[TD([[makeQuery(id+"F0.imprint","IMPRINT",EDGE,{"disambiguationData":[TD([[subQ2,-1.0]])],"derivedFrom":subQ1}),-1.0]])]});}
            var Q11;
            {var subQ0=sQuery(id+"F0.wireOp",EDGE,"E25");Q11=makeQuery(id+"F0.imprint","IMPRINT",FACE,{"disambiguationData":[TD([[makeQuery(id+"F0.imprint","IMPRINT",EDGE,{"derivedFrom":subQ0}),-1.0]])]});}
            var Q12;
            {var subQ0=sQuery(id+"F0.wireOp",EDGE,"E24");var subQ1=sQuery(id+"F0.wireOp",EDGE,"E0");var subQ2=makeQuery(id+"F0.imprint","INTERSECT",VERTEX,{"derivedFrom":[subQ1,subQ0]});Q12=makeQuery(id+"F0.imprint","IMPRINT",FACE,{"disambiguationData":[TD([[makeQuery(id+"F0.imprint","IMPRINT",EDGE,{"disambiguationData":[TD([[subQ2,-1.0]])],"derivedFrom":subQ1}),-1.0]])]});}
            var Q13;
            {var subQ0=sQuery(id+"F0.wireOp",EDGE,"E23");Q13=makeQuery(id+"F0.imprint","IMPRINT",FACE,{"disambiguationData":[TD([[makeQuery(id+"F0.imprint","IMPRINT",EDGE,{"derivedFrom":subQ0}),-1.0]])]});}
            var Q14;
            {var subQ0=sQuery(id+"F0.wireOp",EDGE,"E31");Q14=makeQuery(id+"F0.imprint","IMPRINT",FACE,{"disambiguationData":[TD([[makeQuery(id+"F0.imprint","IMPRINT",EDGE,{"derivedFrom":subQ0}),1.0]])]});}
            var Q15;
            {var subQ0=sQuery(id+"F0.wireOp",EDGE,"E16");var subQ1=sQuery(id+"F0.wireOp",EDGE,"E0");var subQ2=makeQuery(id+"F0.imprint","INTERSECT",VERTEX,{"derivedFrom":[subQ1,subQ0]});Q15=makeQuery(id+"F0.imprint","IMPRINT",FACE,{"disambiguationData":[TD([[makeQuery(id+"F0.imprint","IMPRINT",EDGE,{"disambiguationData":[TD([[subQ2,1.0]])],"derivedFrom":subQ1}),-1.0]])]});}
            var Q16;
            {var subQ0=sQuery(id+"F0.wireOp",EDGE,"E16");var subQ1=sQuery(id+"F0.wireOp",EDGE,"E0");var subQ2=makeQuery(id+"F0.imprint","INTERSECT",VERTEX,{"derivedFrom":[subQ1,subQ0]});Q16=makeQuery(id+"F0.imprint","IMPRINT",FACE,{"disambiguationData":[TD([[makeQuery(id+"F0.imprint","IMPRINT",EDGE,{"disambiguationData":[TD([[subQ2,1.0]])],"derivedFrom":subQ1}),1.0]])]});}
            var Q17;
            {var subQ1=sQuery(id+"F0.wireOp",EDGE,"E36.bottom");Q17=makeQuery(id+"F0.imprint","IMPRINT",FACE,{"disambiguationData":[TD([[makeQuery(id+"F0.imprint","IMPRINT",EDGE,{"derivedFrom":subQ1}),1.0]])]});}
            var Q18;
            {var subQ0=sQuery(id+"F0.wireOp",EDGE,"E36.left");var subQ1=sQuery(id+"F0.wireOp",EDGE,"E1");var subQ2=makeQuery(id+"F0.imprint","INTERSECT",VERTEX,{"disambiguationData":[OD(0.0)],"derivedFrom":[subQ1,subQ0]});Q18=makeQuery(id+"F0.imprint","IMPRINT",FACE,{"disambiguationData":[TD([[makeQuery(id+"F0.imprint","IMPRINT",EDGE,{"disambiguationData":[TD([[subQ2,1.0]])],"derivedFrom":subQ1}),1.0]])]});}
            var Q19;
            {var subQ0=sQuery(id+"F0.wireOp",EDGE,"E30");var subQ1=sQuery(id+"F0.wireOp",EDGE,"E0");var subQ2=makeQuery(id+"F0.imprint","INTERSECT",VERTEX,{"derivedFrom":[subQ1,subQ0]});Q19=makeQuery(id+"F0.imprint","IMPRINT",FACE,{"disambiguationData":[TD([[makeQuery(id+"F0.imprint","IMPRINT",EDGE,{"disambiguationData":[TD([[subQ2,1.0]])],"derivedFrom":subQ1}),-1.0]])]});}
            var Q20;
            {var subQ0=sQuery(id+"F0.wireOp",EDGE,"E29");Q20=makeQuery(id+"F0.imprint","IMPRINT",FACE,{"disambiguationData":[TD([[makeQuery(id+"F0.imprint","IMPRINT",EDGE,{"derivedFrom":subQ0}),1.0]])]});}
            var Q21;
            {var subQ1=sQuery(id+"F0.wireOp",EDGE,"E38.bottom");Q21=makeQuery(id+"F0.imprint","IMPRINT",FACE,{"disambiguationData":[TD([[makeQuery(id+"F0.imprint","IMPRINT",EDGE,{"derivedFrom":subQ1}),1.0]])]});}
            var Q22;
            {var subQ0=sQuery(id+"F0.wireOp",EDGE,"E11");var subQ1=sQuery(id+"F0.wireOp",EDGE,"E0");var subQ2=makeQuery(id+"F0.imprint","INTERSECT",VERTEX,{"derivedFrom":[subQ1,subQ0]});Q22=makeQuery(id+"F0.imprint","IMPRINT",FACE,{"disambiguationData":[TD([[makeQuery(id+"F0.imprint","IMPRINT",EDGE,{"disambiguationData":[TD([[subQ2,-1.0]])],"derivedFrom":subQ1}),-1.0]])]});}
            var Q23;
            {var subQ0=sQuery(id+"F0.wireOp",EDGE,"E25");Q23=makeQuery(id+"F0.imprint","IMPRINT",FACE,{"disambiguationData":[TD([[makeQuery(id+"F0.imprint","IMPRINT",EDGE,{"derivedFrom":subQ0}),-1.0]])]});}
            var Q24;
            {var subQ0=sQuery(id+"F0.wireOp",EDGE,"E11");var subQ1=sQuery(id+"F0.wireOp",EDGE,"E0");var subQ2=makeQuery(id+"F0.imprint","INTERSECT",VERTEX,{"derivedFrom":[subQ1,subQ0]});Q24=makeQuery(id+"F0.imprint","IMPRINT",FACE,{"disambiguationData":[TD([[makeQuery(id+"F0.imprint","IMPRINT",EDGE,{"disambiguationData":[TD([[subQ2,-1.0]])],"derivedFrom":subQ1}),1.0]])]});}
            var Q25;
            {var subQ0=sQuery(id+"F0.wireOp",EDGE,"E24");var subQ1=sQuery(id+"F0.wireOp",EDGE,"E0");var subQ2=makeQuery(id+"F0.imprint","INTERSECT",VERTEX,{"derivedFrom":[subQ1,subQ0]});Q25=makeQuery(id+"F0.imprint","IMPRINT",FACE,{"disambiguationData":[TD([[makeQuery(id+"F0.imprint","IMPRINT",EDGE,{"disambiguationData":[TD([[subQ2,-1.0]])],"derivedFrom":subQ1}),-1.0]])]});}
            var Q26;
            {var subQ0=sQuery(id+"F0.wireOp",EDGE,"E23");Q26=makeQuery(id+"F0.imprint","IMPRINT",FACE,{"disambiguationData":[TD([[makeQuery(id+"F0.imprint","IMPRINT",EDGE,{"derivedFrom":subQ0}),-1.0]])]});}
            var Q27;
            {var subQ0=sQuery(id+"F0.wireOp",EDGE,"E27");var subQ1=sQuery(id+"F0.wireOp",EDGE,"E1");var subQ2=makeQuery(id+"F0.imprint","INTERSECT",VERTEX,{"disambiguationData":[OD(0.0)],"derivedFrom":[subQ1,subQ0]});Q27=makeQuery(id+"F0.imprint","IMPRINT",FACE,{"disambiguationData":[TD([[makeQuery(id+"F0.imprint","IMPRINT",EDGE,{"disambiguationData":[TD([[subQ2,-1.0]])],"derivedFrom":subQ1}),1.0]])]});}
            extrude(context, id + "F14", {"entities" : qUnion([Q0, Q1, Q2, Q3, Q4, Q5, Q6, Q7, Q8, Q9, Q10, Q11, Q12, Q13, Q14, Q15, Q16, Q17, Q18, Q19, Q20, Q21, Q22, Q23, Q24, Q25, Q26, Q27]), "oppositeDirection" : true, "depth" : 50.8 * mm});
        }
        {
            var Q0;
            Q0=makeQuery(id+"F14.opExtrude","SWEPT_BODY",BODY,{"disambiguationData":[OSD([sQuery(id+"F0.wireOp",EDGE,"E30"),sQuery(id+"F0.wireOp",EDGE,"E32"),sQuery(id+"F0.wireOp",EDGE,"E33"),sQuery(id+"F0.wireOp",EDGE,"E34")])]});
            var Q1;
            Q1=makeQuery(id+"F14.opExtrude","SWEPT_BODY",BODY,{"disambiguationData":[OSD([sQuery(id+"F0.wireOp",EDGE,"E12"),sQuery(id+"F0.wireOp",EDGE,"E13"),sQuery(id+"F0.wireOp",EDGE,"E14"),sQuery(id+"F0.wireOp",EDGE,"E15"),sQuery(id+"F0.wireOp",EDGE,"E16")])]});
            var Q2;
            Q2=makeQuery(id+"F14.opExtrude","SWEPT_BODY",BODY,{"disambiguationData":[OSD([sQuery(id+"F0.wireOp",EDGE,"E7"),sQuery(id+"F0.wireOp",EDGE,"E8"),sQuery(id+"F0.wireOp",EDGE,"E9"),sQuery(id+"F0.wireOp",EDGE,"E10"),sQuery(id+"F0.wireOp",EDGE,"E11")])]});
            var Q3;
            Q3=makeQuery(id+"F14.opExtrude","SWEPT_BODY",BODY,{"disambiguationData":[OSD([sQuery(id+"F0.wireOp",EDGE,"E24"),sQuery(id+"F0.wireOp",EDGE,"E26"),sQuery(id+"F0.wireOp",EDGE,"E27"),sQuery(id+"F0.wireOp",EDGE,"E28")])]});
            var Q4;
            Q4=makeQuery(id+"F14.opExtrude","SWEPT_BODY",BODY,{"disambiguationData":[OSD([sQuery(id+"F0.wireOp",EDGE,"E39.bottom"),sQuery(id+"F0.wireOp",EDGE,"E39.top"),sQuery(id+"F0.wireOp",EDGE,"E38.right"),sQuery(id+"F0.wireOp",EDGE,"E39.right")])]});
            var Q5;
            Q5=makeQuery(id+"F14.opExtrude","SWEPT_BODY",BODY,{"disambiguationData":[OSD([sQuery(id+"F0.wireOp",EDGE,"E37.bottom"),sQuery(id+"F0.wireOp",EDGE,"E37.top"),sQuery(id+"F0.wireOp",EDGE,"E36.right"),sQuery(id+"F0.wireOp",EDGE,"E37.right")])]});
            transform(context, id + "F15", {"entities" : qUnion([Q0, Q1, Q2, Q3, Q4, Q5]), "transformType" : TransformType.TRANSLATION_3D, "dx" : 0 * mm, "dy" : -254 * mm, "dz" : 0 * mm, "makeCopy" : true});
        }
        {
            var Q0;
            Q0=makeQuery(id+"F6.opExtrude","SWEPT_BODY",BODY,{"disambiguationData":[OSD([sQuery(id+"F5.wireOp",EDGE,"E42"),sQuery(id+"F5.wireOp",EDGE,"E44.top"),sQuery(id+"F5.wireOp",EDGE,"E44.right")])]});
            var Q1;
            Q1=makeQuery(id+"F6.opExtrude","SWEPT_BODY",BODY,{"disambiguationData":[OSD([sQuery(id+"F5.wireOp",EDGE,"E42"),sQuery(id+"F5.wireOp",EDGE,"E44.bottom"),sQuery(id+"F5.wireOp",EDGE,"E44.right")])]});
            var Q2;
            Q2=makeQuery(id+"F6.opExtrude","SWEPT_BODY",BODY,{"disambiguationData":[OSD([sQuery(id+"F5.wireOp",EDGE,"E41")])]});
            var Q3;
            Q3=makeQuery(id+"F8.opExtrude","SWEPT_BODY",BODY,{"disambiguationData":[OSD([sQuery(id+"F5.wireOp",EDGE,"E46"),sQuery(id+"F5.wireOp",EDGE,"E50.bottom"),sQuery(id+"F5.wireOp",EDGE,"E50.top"),sQuery(id+"F5.wireOp",EDGE,"E50.right")])]});
            var Q4;
            Q4=makeQuery(id+"F8.opExtrude","SWEPT_BODY",BODY,{"disambiguationData":[OSD([sQuery(id+"F5.wireOp",EDGE,"E47")])]});
            var Q5;
            Q5=makeQuery(id+"F15.opPattern","COPY",BODY,{"derivedFrom":makeQuery(id+"F14.opExtrude","SWEPT_BODY",BODY,{"disambiguationData":[OSD([sQuery(id+"F0.wireOp",EDGE,"E30"),sQuery(id+"F0.wireOp",EDGE,"E32"),sQuery(id+"F0.wireOp",EDGE,"E33"),sQuery(id+"F0.wireOp",EDGE,"E34")])]}),"instanceName":"1"});
            var Q6;
            Q6=makeQuery(id+"F15.opPattern","COPY",BODY,{"derivedFrom":makeQuery(id+"F14.opExtrude","SWEPT_BODY",BODY,{"disambiguationData":[OSD([sQuery(id+"F0.wireOp",EDGE,"E7"),sQuery(id+"F0.wireOp",EDGE,"E8"),sQuery(id+"F0.wireOp",EDGE,"E9"),sQuery(id+"F0.wireOp",EDGE,"E10"),sQuery(id+"F0.wireOp",EDGE,"E11")])]}),"instanceName":"1"});
            var Q7;
            Q7=makeQuery(id+"F15.opPattern","COPY",BODY,{"derivedFrom":makeQuery(id+"F14.opExtrude","SWEPT_BODY",BODY,{"disambiguationData":[OSD([sQuery(id+"F0.wireOp",EDGE,"E12"),sQuery(id+"F0.wireOp",EDGE,"E13"),sQuery(id+"F0.wireOp",EDGE,"E14"),sQuery(id+"F0.wireOp",EDGE,"E15"),sQuery(id+"F0.wireOp",EDGE,"E16")])]}),"instanceName":"1"});
            var Q8;
            Q8=makeQuery(id+"F15.opPattern","COPY",BODY,{"derivedFrom":makeQuery(id+"F14.opExtrude","SWEPT_BODY",BODY,{"disambiguationData":[OSD([sQuery(id+"F0.wireOp",EDGE,"E24"),sQuery(id+"F0.wireOp",EDGE,"E26"),sQuery(id+"F0.wireOp",EDGE,"E27"),sQuery(id+"F0.wireOp",EDGE,"E28")])]}),"instanceName":"1"});
            var Q9;
            Q9=makeQuery(id+"F14.opExtrude","SWEPT_BODY",BODY,{"disambiguationData":[OSD([sQuery(id+"F0.wireOp",EDGE,"E30"),sQuery(id+"F0.wireOp",EDGE,"E32"),sQuery(id+"F0.wireOp",EDGE,"E33"),sQuery(id+"F0.wireOp",EDGE,"E34")])]});
            var Q10;
            Q10=makeQuery(id+"F14.opExtrude","SWEPT_BODY",BODY,{"disambiguationData":[OSD([sQuery(id+"F0.wireOp",EDGE,"E12"),sQuery(id+"F0.wireOp",EDGE,"E13"),sQuery(id+"F0.wireOp",EDGE,"E14"),sQuery(id+"F0.wireOp",EDGE,"E15"),sQuery(id+"F0.wireOp",EDGE,"E16")])]});
            var Q11;
            Q11=makeQuery(id+"F14.opExtrude","SWEPT_BODY",BODY,{"disambiguationData":[OSD([sQuery(id+"F0.wireOp",EDGE,"E7"),sQuery(id+"F0.wireOp",EDGE,"E8"),sQuery(id+"F0.wireOp",EDGE,"E9"),sQuery(id+"F0.wireOp",EDGE,"E10"),sQuery(id+"F0.wireOp",EDGE,"E11")])]});
            var Q12;
            Q12=makeQuery(id+"F14.opExtrude","SWEPT_BODY",BODY,{"disambiguationData":[OSD([sQuery(id+"F0.wireOp",EDGE,"E24"),sQuery(id+"F0.wireOp",EDGE,"E26"),sQuery(id+"F0.wireOp",EDGE,"E27"),sQuery(id+"F0.wireOp",EDGE,"E28")])]});
            var Q13;
            Q13=makeQuery(id+"F14.opExtrude","SWEPT_BODY",BODY,{"disambiguationData":[OSD([sQuery(id+"F0.wireOp",EDGE,"E37.bottom"),sQuery(id+"F0.wireOp",EDGE,"E37.top"),sQuery(id+"F0.wireOp",EDGE,"E36.right"),sQuery(id+"F0.wireOp",EDGE,"E37.right")])]});
            var Q14;
            Q14=makeQuery(id+"F14.opExtrude","SWEPT_BODY",BODY,{"disambiguationData":[OSD([sQuery(id+"F0.wireOp",EDGE,"E39.bottom"),sQuery(id+"F0.wireOp",EDGE,"E39.top"),sQuery(id+"F0.wireOp",EDGE,"E38.right"),sQuery(id+"F0.wireOp",EDGE,"E39.right")])]});
            var Q15;
            Q15=makeQuery(id+"F15.opPattern","COPY",BODY,{"derivedFrom":makeQuery(id+"F14.opExtrude","SWEPT_BODY",BODY,{"disambiguationData":[OSD([sQuery(id+"F0.wireOp",EDGE,"E36.bottom"),sQuery(id+"F0.wireOp",EDGE,"E36.top"),sQuery(id+"F0.wireOp",EDGE,"E36.left"),sQuery(id+"F0.wireOp",EDGE,"E36.right")])]}),"instanceName":"1"});
            var Q16;
            Q16=makeQuery(id+"F15.opPattern","COPY",BODY,{"derivedFrom":makeQuery(id+"F14.opExtrude","SWEPT_BODY",BODY,{"disambiguationData":[OSD([sQuery(id+"F0.wireOp",EDGE,"E38.bottom"),sQuery(id+"F0.wireOp",EDGE,"E38.top"),sQuery(id+"F0.wireOp",EDGE,"E27"),sQuery(id+"F0.wireOp",EDGE,"E38.right")])]}),"instanceName":"1"});
            booleanBodies(context, id + "F16", {"operationType" : BooleanOperationType.SUBTRACTION, "tools" : qUnion([Q0, Q1, Q2, Q3, Q4]), "targets" : qUnion([Q5, Q6, Q7, Q8, Q9, Q10, Q11, Q12, Q13, Q14, Q15, Q16])});
        }
        {
            var Q0;
            {var subQ5=sQuery(id+"F5.wireOp",EDGE,"E50.right");Q0=makeQuery(id+"F5.imprint","IMPRINT",FACE,{"disambiguationData":[TD([[makeQuery(id+"F5.imprint","IMPRINT",EDGE,{"derivedFrom":subQ5}),1.0]])]});}
            var Q1;
            {var subQ0=sQuery(id+"F5.wireOp",EDGE,"E44.top");var subQ1=sQuery(id+"F5.wireOp",EDGE,"E42");var subQ2=makeQuery(id+"F5.imprint","INTERSECT",VERTEX,{"derivedFrom":[subQ1,subQ0]});Q1=makeQuery(id+"F5.imprint","IMPRINT",FACE,{"disambiguationData":[TD([[makeQuery(id+"F5.imprint","IMPRINT",EDGE,{"disambiguationData":[TD([[subQ2,1.0]])],"derivedFrom":subQ1}),-1.0]])]});}
            var Q2;
            {var subQ0=sQuery(id+"F5.wireOp",EDGE,"E44.right");var subQ1=sQuery(id+"F5.wireOp",EDGE,"E42");var subQ2=makeQuery(id+"F5.imprint","INTERSECT",VERTEX,{"derivedFrom":[subQ1,subQ0]});Q2=makeQuery(id+"F5.imprint","IMPRINT",FACE,{"disambiguationData":[TD([[makeQuery(id+"F5.imprint","IMPRINT",EDGE,{"disambiguationData":[TD([[subQ2,1.0]])],"derivedFrom":subQ1}),-1.0]])]});}
            extrude(context, id + "F17", {"entities" : qUnion([Q0, Q1, Q2]), "endBound" : BoundingType.SYMMETRIC, "depth" : 127 * mm});
        }
        {
            var Q0;
            {var subQ0=sQuery(id+"F5.wireOp",EDGE,"E52");Q0=makeQuery(id+"F5.imprint","IMPRINT",FACE,{"disambiguationData":[TD([[makeQuery(id+"F5.imprint","IMPRINT",EDGE,{"derivedFrom":subQ0}),-1.0]])]});}
            extrude(context, id + "F18", {"entities" : qUnion([Q0]), "endBound" : BoundingType.SYMMETRIC, "depth" : 19.05 * mm});
        }
        {
            var Q0;
            {var subQ0=sQuery(id+"F5.wireOp",EDGE,"E52");Q0=makeQuery(id+"F5.imprint","IMPRINT",FACE,{"disambiguationData":[TD([[makeQuery(id+"F5.imprint","IMPRINT",EDGE,{"derivedFrom":subQ0}),-1.0]])]});}
            extrude(context, id + "F19", {"entities" : qUnion([Q0]), "endBound" : BoundingType.SYMMETRIC, "depth" : 6.35 * mm});
        }
        {
            var Q0;
            Q0=makeQuery(id+"F19.opExtrude","SWEPT_BODY",BODY,{"disambiguationData":[OSD([sQuery(id+"F5.wireOp",EDGE,"E52"),sQuery(id+"F5.wireOp",EDGE,"E55.left"),sQuery(id+"F5.wireOp",EDGE,"E61")])]});
            var Q1;
            Q1=makeQuery(id+"F18.opExtrude","SWEPT_BODY",BODY,{"disambiguationData":[OSD([sQuery(id+"F5.wireOp",EDGE,"E52"),sQuery(id+"F5.wireOp",EDGE,"E55.left"),sQuery(id+"F5.wireOp",EDGE,"E61")])]});
            booleanBodies(context, id + "F20", {"operationType" : BooleanOperationType.SUBTRACTION, "tools" : qUnion([Q0]), "targets" : qUnion([Q1])});
        }
        {
            var Q0;
            Q0=makeQuery(id+"F14.opExtrude","SWEPT_BODY",BODY,{"disambiguationData":[OSD([sQuery(id+"F0.wireOp",EDGE,"E7"),sQuery(id+"F0.wireOp",EDGE,"E11"),sQuery(id+"F0.wireOp",EDGE,"E23"),sQuery(id+"F0.wireOp",EDGE,"E24"),sQuery(id+"F0.wireOp",EDGE,"E25")])]});
            deleteBodies(context, id + "F21", {"entities" : qUnion([Q0])});
        }
        {
            var Q0;
            Q0=makeQuery(id+"F14.opExtrude","SWEPT_BODY",BODY,{"disambiguationData":[OSD([sQuery(id+"F0.wireOp",EDGE,"E12"),sQuery(id+"F0.wireOp",EDGE,"E16"),sQuery(id+"F0.wireOp",EDGE,"E29"),sQuery(id+"F0.wireOp",EDGE,"E30"),sQuery(id+"F0.wireOp",EDGE,"E31")])]});
            var Q1;
            Q1=makeQuery(id+"F14.opExtrude","SWEPT_BODY",BODY,{"disambiguationData":[OSD([sQuery(id+"F0.wireOp",EDGE,"E36.bottom"),sQuery(id+"F0.wireOp",EDGE,"E36.top"),sQuery(id+"F0.wireOp",EDGE,"E36.left"),sQuery(id+"F0.wireOp",EDGE,"E36.right")])]});
            var Q2;
            Q2=makeQuery(id+"F14.opExtrude","SWEPT_BODY",BODY,{"disambiguationData":[OSD([sQuery(id+"F0.wireOp",EDGE,"E38.bottom"),sQuery(id+"F0.wireOp",EDGE,"E38.top"),sQuery(id+"F0.wireOp",EDGE,"E27"),sQuery(id+"F0.wireOp",EDGE,"E38.right")])]});
            deleteBodies(context, id + "F22", {"entities" : qUnion([Q0, Q1, Q2])});
        }
        {
            var Q0;
            Q0=makeQuery(id+"F3.opExtrude","SWEPT_BODY",BODY,{"disambiguationData":[OSD([sQuery(id+"F0.wireOp",EDGE,"E0"),sQuery(id+"F0.wireOp",EDGE,"E7"),sQuery(id+"F0.wireOp",EDGE,"E11"),sQuery(id+"F0.wireOp",EDGE,"E23"),sQuery(id+"F0.wireOp",EDGE,"E24"),sQuery(id+"F0.wireOp",EDGE,"E25"),sQuery(id+"F0.wireOp",EDGE,"E26"),sQuery(id+"F0.wireOp",EDGE,"E28"),sQuery(id+"F0.wireOp",EDGE,"E38.bottom"),sQuery(id+"F0.wireOp",EDGE,"E38.top"),sQuery(id+"F0.wireOp",EDGE,"E38.right")])]});
            var Q1;
            Q1=makeQuery(id+"F3.opExtrude","SWEPT_BODY",BODY,{"disambiguationData":[OSD([sQuery(id+"F0.wireOp",EDGE,"E0"),sQuery(id+"F0.wireOp",EDGE,"E12"),sQuery(id+"F0.wireOp",EDGE,"E16"),sQuery(id+"F0.wireOp",EDGE,"E29"),sQuery(id+"F0.wireOp",EDGE,"E30"),sQuery(id+"F0.wireOp",EDGE,"E31"),sQuery(id+"F0.wireOp",EDGE,"E32"),sQuery(id+"F0.wireOp",EDGE,"E34"),sQuery(id+"F0.wireOp",EDGE,"E36.bottom"),sQuery(id+"F0.wireOp",EDGE,"E36.top"),sQuery(id+"F0.wireOp",EDGE,"E36.right")])]});
            deleteBodies(context, id + "F23", {"entities" : qUnion([Q0, Q1])});
        }
        {
            var Q0;
            Q0=qCreatedBy(makeId("Right.planeOp"),FACE);
            var sketch = newSketch(context, id + "F24", { "sketchPlane" : qUnion([Q0])});
            skLineSegment(sketch, "E67", {"start": v(0, 0) * mm, "end": v(0, 48.26) * mm});
            skLineSegment(sketch, "E68", {"start": v(0, 48.26) * mm, "end": v(6.35, 48.26) * mm});
            skLineSegment(sketch, "E69", {"start": v(6.35, 48.26) * mm, "end": v(6.35, 44.77) * mm});
            skLineSegment(sketch, "E70", {"start": v(6.35, 44.77) * mm, "end": v(13.34, 44.77) * mm});
            skLineSegment(sketch, "E71", {"start": v(13.34, 44.77) * mm, "end": v(13.34, 48.26) * mm});
            skLineSegment(sketch, "E72", {"start": v(13.34, 48.26) * mm, "end": v(19.69, 48.26) * mm});
            skLineSegment(sketch, "E73", {"start": v(19.69, 48.26) * mm, "end": v(19.69, 41.91) * mm});
            skLineSegment(sketch, "E74", {"start": v(19.69, 41.91) * mm, "end": v(6.35, 41.91) * mm});
            skLineSegment(sketch, "E75", {"start": v(6.35, 41.91) * mm, "end": v(0, 41.91) * mm});
            skLineSegment(sketch, "E76", {"start": v(0, 41.91) * mm, "end": v(0, 48.26) * mm});
            skLineSegment(sketch, "E77", {"start": v(0, 48.26) * mm, "end": v(3.18, 48.26) * mm});
            skLineSegment(sketch, "E78", {"start": v(3.18, 48.26) * mm, "end": v(3.18, 51.75) * mm});
            skLineSegment(sketch, "E79", {"start": v(3.18, 51.75) * mm, "end": v(19.69, 51.75) * mm});
            skLineSegment(sketch, "E80", {"start": v(19.69, 51.75) * mm, "end": v(19.69, 54.93) * mm});
            skLineSegment(sketch, "E81", {"start": v(19.69, 54.93) * mm, "end": v(0, 54.93) * mm});
            skLineSegment(sketch, "E82", {"start": v(0, 54.93) * mm, "end": v(0, 48.26) * mm});
            skLineSegment(sketch, "E83.bottom", {"start": v(0, 48.26) * mm, "end": v(-25.4, 48.26) * mm});
            skLineSegment(sketch, "E83.top", {"start": v(0, 54.93) * mm, "end": v(-25.4, 54.93) * mm});
            skLineSegment(sketch, "E83.left", {"start": v(0, 48.26) * mm, "end": v(0, 54.93) * mm});
            skLineSegment(sketch, "E83.right", {"start": v(-25.4, 48.26) * mm, "end": v(-25.4, 54.93) * mm});
            skSolve(sketch);
        }
        {
            var Q0;
            Q0=makeQuery(id+"F24.imprint","IMPRINT",FACE,{"disambiguationData":[TD([[makeQuery(id+"F24.imprint","IMPRINT",EDGE,{"derivedFrom":sQuery(id+"F24.wireOp",EDGE,"E77")}),1.0]])]});
            var Q1;
            Q1=makeQuery(id+"F24.imprint","IMPRINT",FACE,{"disambiguationData":[TD([[makeQuery(id+"F24.imprint","IMPRINT",EDGE,{"derivedFrom":sQuery(id+"F24.wireOp",EDGE,"E68")}),-1.0]])]});
            var Q2;
            Q2=makeQuery(id+"F24.imprint","IMPRINT",FACE,{"disambiguationData":[TD([[makeQuery(id+"F24.imprint","IMPRINT",EDGE,{"derivedFrom":sQuery(id+"F24.wireOp",EDGE,"E83.bottom")}),-1.0]])]});
            var Q3;
            Q3=sQuery(id+"F5.wireOp",EDGE,"E40");
            revolve(context, id + "F25", {"entities" : qUnion([Q0, Q1, Q2]), "axis" : qUnion([Q3]), "revolveType" : RevolveType.FULL});
        }
        {
            var Q0;
            Q0=makeQuery(id+"F17.opExtrude","SWEPT_BODY",BODY,{"disambiguationData":[OSD([sQuery(id+"F5.wireOp",EDGE,"E42"),sQuery(id+"F5.wireOp",EDGE,"E44.top"),sQuery(id+"F5.wireOp",EDGE,"E44.right")])]});
            var Q1;
            Q1=makeQuery(id+"F17.opExtrude","SWEPT_BODY",BODY,{"disambiguationData":[OSD([sQuery(id+"F5.wireOp",EDGE,"E42"),sQuery(id+"F5.wireOp",EDGE,"E44.bottom"),sQuery(id+"F5.wireOp",EDGE,"E44.right")])]});
            var Q2;
            Q2=makeQuery(id+"F17.opExtrude","SWEPT_BODY",BODY,{"disambiguationData":[OSD([sQuery(id+"F5.wireOp",EDGE,"E46"),sQuery(id+"F5.wireOp",EDGE,"E50.bottom"),sQuery(id+"F5.wireOp",EDGE,"E50.top"),sQuery(id+"F5.wireOp",EDGE,"E50.right")])]});
            deleteBodies(context, id + "F26", {"entities" : qUnion([Q0, Q1, Q2])});
        }
    });
